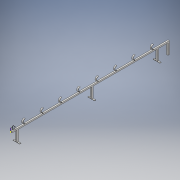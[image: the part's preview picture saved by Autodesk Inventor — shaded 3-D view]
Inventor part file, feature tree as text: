
AUTODESK INVENTOR PART (.ipt)
format: ipt  version: 2017 (Build 210142000, 142)  size: 228,864 bytes
history: native  units: mm
features: sketch x8, extrude x7, pattern_linear x3
ambient origin geometry x8: Origin, YZ Plane, XZ Plane, XY Plane, X Axis, Y Axis, Z Axis, Center Point
bodies: Solid1 (feature_tree)
feature tree (18):
  extrude  "Extrusion1"  Depth=2900.0mm
  extrude  "Extrusion2"  Depth=25.0mm
  extrude  "Extrusion5"  Depth=5.0mm
  extrude  "Extrusion6"  Depth=50.0mm TaperAngle=0.0deg
  extrude  "Extrusion7"  Depth=50.0mm TaperAngle=0.0deg
  pattern_linear  "Rectangular Pattern3"  Count1=8 Spacing1=338.0mm
  sketch  "Sketch10"  dims[d31=4.0mm]
  extrude  "Extrusion8"  Depth=290.0mm
  pattern_linear  "Rectangular Pattern4"  Spacing1=42.0mm  [1 undecoded]
  pattern_linear  "Rectangular Pattern5"  Spacing1=25.0mm  [1 undecoded]
  extrude  "Extrusion9"  Depth=25.0mm
  sketch  "Sketch1"  dims[d0=25.0mm d1=2900.0mm]
  sketch  "Sketch2"  dims[d2=25.0mm d3=0.0mm d4=25.0mm]
  sketch  "Sketch6"  dims[d5=200.0mm d6=0.0mm d13=5.0mm]
  sketch  "Sketch7"  dims[d14=25.0mm d15=50.0mm d16=75.0mm d17=0.0mm d18=0.0mm]
  sketch  "Sketch8"  dims[d22=5.0mm d23=50.0mm d24=75.0mm d25=0.0mm d26=0.0mm]
  sketch  "Sketch11"  dims[d32=25.0mm d33=0.0mm d34=80.0mm d36=338.0mm]
  sketch  "Sketch12"  dims[d39=42.0mm d40=290.0mm d41=42.0mm d42=25.0mm d43=25.0mm d44=10.0mm d45=0.0mm d46=20.0mm d48=1204.0mm d49=0.0mm d50=20.0mm d52=1379.0mm d53=25.0mm d54=25.0mm d55=0.0mm d56=10.0mm d57=0.0mm]
note: 2 required parameter values undecoded (feature->parameter linkage not recoverable at this tier; creation-order binding heuristic only, values carry confidence <= 0.55)
